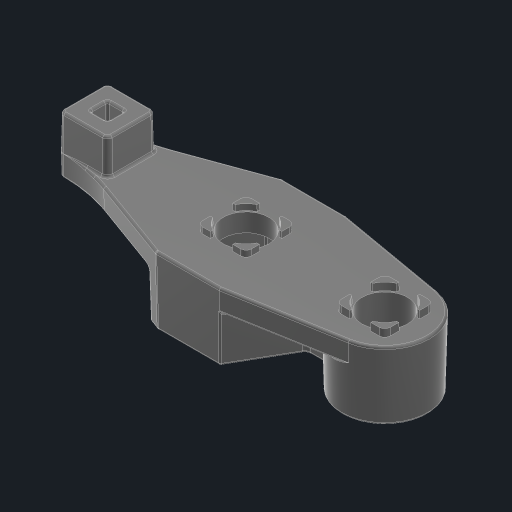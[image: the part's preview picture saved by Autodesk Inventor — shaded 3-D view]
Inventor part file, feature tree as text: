
AUTODESK INVENTOR PART (.ipt)
format: ipt  version: 2023 (Build 270158030, 158C)  size: 737,280 bytes
history: native  units: in
note: dims shown in document units (in); Inventor stores cm internally (conversion verified against a paired STEP export)
features: extrude x1, sketch x1, fillet x1
ambient origin geometry x8: Origin, YZ Plane, XZ Plane, XY Plane, X Axis, Y Axis, Z Axis, Center Point
bodies: Solid1 (feature_tree)
feature tree (3):
  extrude  "Extrusion1"  [1 undecoded]
  sketch  "Sketch1"  dims[d4=1.0in d5=0.0in]
  fillet  "Fillet15"  [1 undecoded]
note: 2 required parameter values undecoded (feature->parameter linkage not recoverable at this tier; creation-order binding heuristic only, values carry confidence <= 0.55)
